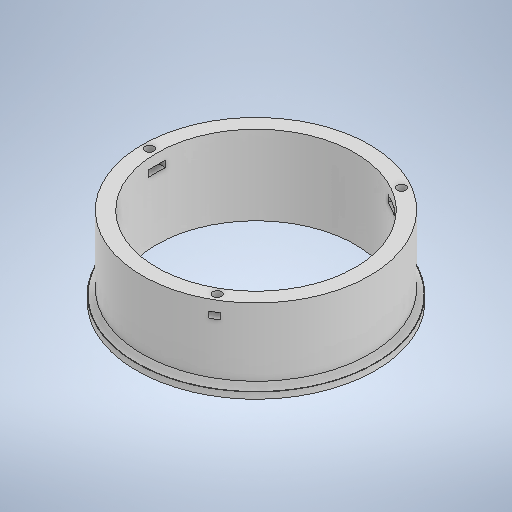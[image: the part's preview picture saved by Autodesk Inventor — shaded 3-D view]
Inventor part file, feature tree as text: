
AUTODESK INVENTOR PART (.ipt)
format: ipt  version: 2025 (Build 290162000, 162)  size: 296,960 bytes
history: native  units: mm
features: sketch x5, extrude x4, pattern_circular x2, hole x1, chamfer x1
ambient origin geometry x8: Origin, YZ Plane, XZ Plane, XY Plane, X Axis, Y Axis, Z Axis, Center Point
bodies: Solid1 (feature_tree)
feature tree (13):
  extrude  "Base"  Depth=30.0mm TaperAngle=0.0deg
  extrude  "Nut Seat"  Depth=108.9mm
  pattern_circular  "Circular Pattern1"  Count=3 Angle=360.0deg
  extrude  "Top Slice"  Depth=3.0mm
  hole  "Hole1"  [1 undecoded]
  pattern_circular  "Circular Pattern2"  [2 undecoded]
  extrude  "Lip"  Depth=3.0mm TaperAngle=45.0deg
  chamfer  "Chamfer 1"  Distance=0.5mm
  sketch  "Sketch1"  dims[d0=102.0mm d3=30.0mm d4=0.0mm]
  sketch  "Sketch2"  dims[d6=95.1mm d7=108.9mm]
  sketch  "Sketch3"  dims[d8=3.0mm d9=0.0mm d10=30.0mm d11=360.0deg]
  sketch  "Sketch4"  dims[d13=5.0mm d14=0.0mm]
  sketch  "Sketch5"  dims[d15=4.2mm d16=6.0mm d17=4.0mm d18=2.0mm d19=90.0deg d20=8.0mm d21=0.0mm d22=51.0mm d23=30.0mm d24=360.0deg d26=3.0mm d27=0.0mm d31=2.5mm d32=2.0mm d33=45.0deg d12=0.5mm]
note: 3 required parameter values undecoded (feature->parameter linkage not recoverable at this tier; creation-order binding heuristic only, values carry confidence <= 0.55)
